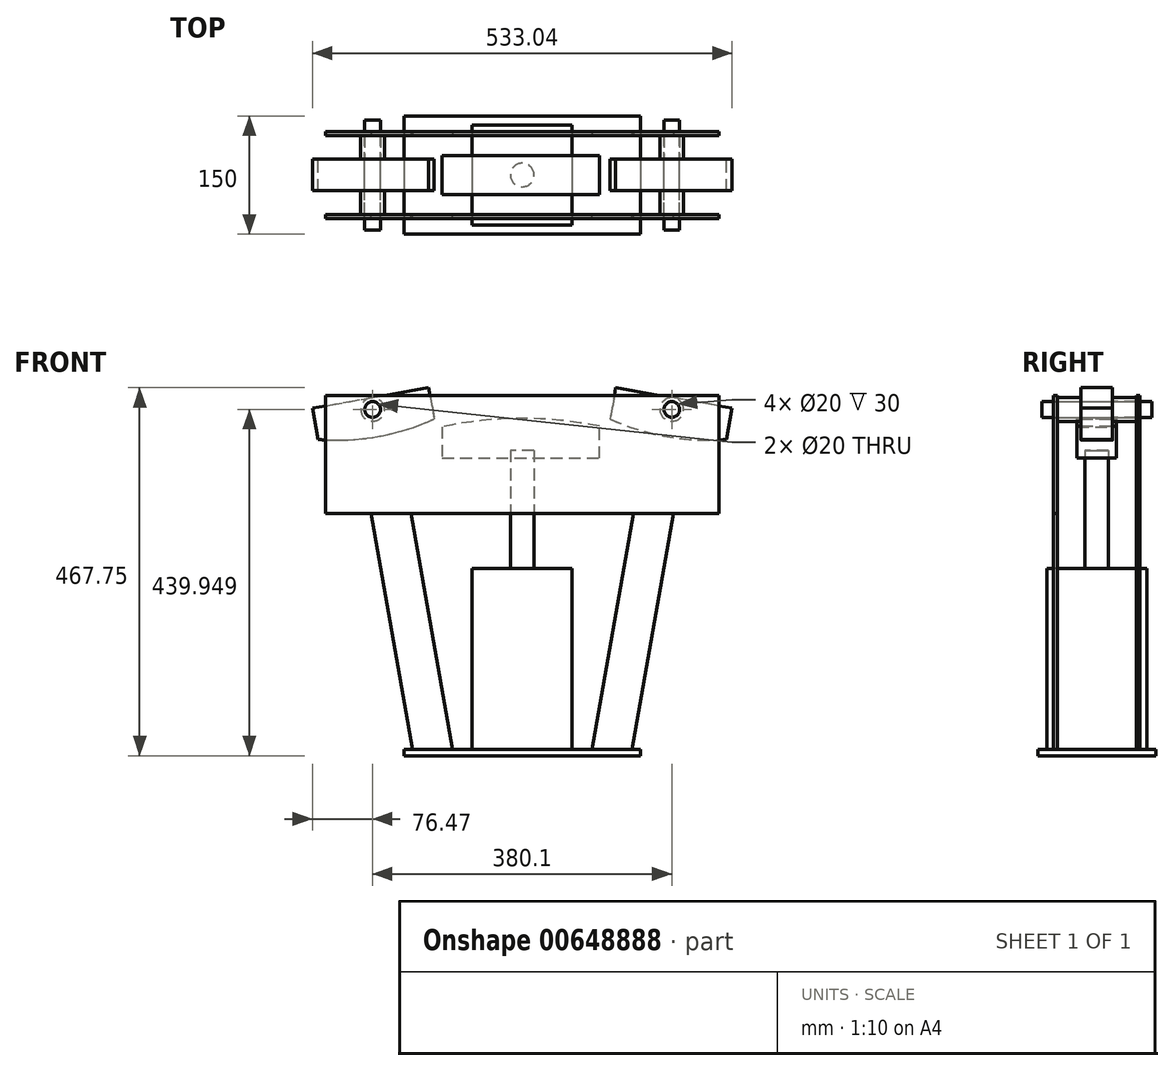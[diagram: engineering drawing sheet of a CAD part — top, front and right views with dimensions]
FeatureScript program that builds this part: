
annotation { "Feature Type Name" : "Feature", "Feature Type Description" : "" }
export const myFeature = defineFeature(function(context is Context, id is Id, definition is map)
    precondition{}
    {
        {
            var Q0;
            Q0=qCreatedBy(makeId("Top.planeOp"),FACE);
            cPlane(context, id + "F0", {"entities" : qUnion([Q0]), "cplaneType" : CPlaneType.OFFSET, "offset" : (250 + 127) * mm, "oppositeDirection" : true, "width" : 150 * mm, "height" : 150 * mm});
        }
        {
            var Q0;
            Q0=qCreatedBy(id+"F0.planeOp",FACE);
            var sketch = newSketch(context, id + "F1", { "sketchPlane" : qUnion([Q0])});
            skLineSegment(sketch, "E0.bottom", {"start": v(63.5, 63.5) * mm, "end": v(-63.5, 63.5) * mm});
            skLineSegment(sketch, "E0.top", {"start": v(63.5, -63.5) * mm, "end": v(-63.5, -63.5) * mm});
            skLineSegment(sketch, "E0.left", {"start": v(63.5, 63.5) * mm, "end": v(63.5, -63.5) * mm});
            skLineSegment(sketch, "E0.right", {"start": v(-63.5, 63.5) * mm, "end": v(-63.5, -63.5) * mm});
            skPoint(sketch, "E0.middle", {"position": v(0, 0) * mm});
            skSolve(sketch);
        }
        {
            var Q0;
            Q0=qSketchRegion(id+"F1",true);
            extrude(context, id + "F2", {"entities" : qUnion([Q0]), "depth" : 230 * mm, "offsetDistance" : 25 * mm});
        }
        {
            var Q0;
            Q0=makeQuery(id+"F2.opExtrude","CAP_FACE",FACE,{"disambiguationData":[OSD([sQuery(id+"F1.wireOp",EDGE,"E0.bottom"),sQuery(id+"F1.wireOp",EDGE,"E0.top"),sQuery(id+"F1.wireOp",EDGE,"E0.left"),sQuery(id+"F1.wireOp",EDGE,"E0.right")])],"isStart":false});
            var sketch = newSketch(context, id + "F3", { "sketchPlane" : qUnion([Q0])});
            skCircle(sketch, "E1", {"center": v(0, 0) * mm, "radius": 15 * mm});
            skSolve(sketch);
        }
        {
            var Q0;
            Q0=qSketchRegion(id+"F3",true);
            extrude(context, id + "F4", {"entities" : qUnion([Q0]), "depth" : 150 * mm, "offsetDistance" : 25 * mm});
        }
        {
            var Q0;
            Q0=qCreatedBy(id+"F0.planeOp",FACE);
            var sketch = newSketch(context, id + "F5", { "sketchPlane" : qUnion([Q0])});
            skLineSegment(sketch, "E2.bottom", {"start": v(150, 75) * mm, "end": v(-150, 75) * mm});
            skLineSegment(sketch, "E2.top", {"start": v(150, -75) * mm, "end": v(-150, -75) * mm});
            skLineSegment(sketch, "E2.left", {"start": v(150, 75) * mm, "end": v(150, -75) * mm});
            skLineSegment(sketch, "E2.right", {"start": v(-150, 75) * mm, "end": v(-150, -75) * mm});
            skPoint(sketch, "E2.middle", {"position": v(0, 0) * mm});
            skSolve(sketch);
        }
        {
            var Q0;
            Q0=qSketchRegion(id+"F5",true);
            extrude(context, id + "F6", {"entities" : qUnion([Q0]), "oppositeDirection" : true, "depth" : 8 * mm, "offsetDistance" : 25 * mm});
        }
        {
            var Q0;
            Q0=qCreatedBy(makeId("Front.planeOp"),FACE);
            var sketch = newSketch(context, id + "F7", { "sketchPlane" : qUnion([Q0])});
            skArc(sketch, "E3", {"start": v(-101.76, 33) * mm, "mid": v(-1.8, 43.46) * mm, "end": v(98.24, 33.72) * mm});
            skLineSegment(sketch, "E4", {"start": v(-101.76, 33) * mm, "end": v(-101.76, -7) * mm});
            skLineSegment(sketch, "E5", {"start": v(-101.76, -7) * mm, "end": v(98.24, -7) * mm});
            skLineSegment(sketch, "E6", {"start": v(98.24, -7) * mm, "end": v(98.24, 33.72) * mm});
            skSolve(sketch);
        }
        {
            var Q0;
            Q0 = qSketchRegion(id + "F7", true);
            extrude(context, id + "F8", {"entities" : qUnion([Q0]), "endBound" : BoundingType.SYMMETRIC, "depth" : 50 * mm, "offsetDistance" : 25 * mm});
        }
        {
            var Q0;
            Q0=qCreatedBy(makeId("Front.planeOp"),FACE);
            cPlane(context, id + "F9", {"entities" : qUnion([Q0]), "cplaneType" : CPlaneType.OFFSET, "offset" : 50 * mm, "width" : 150 * mm, "height" : 150 * mm});
        }
        {
            var Q0;
            Q0=qCreatedBy(id+"F9.planeOp",FACE);
            var sketch = newSketch(context, id + "F10", { "sketchPlane" : qUnion([Q0])});
            skLineSegment(sketch, "E7", {"start": v(-88.5, -377) * mm, "end": v(-141.4, -77) * mm});
            skLineSegment(sketch, "E8", {"start": v(-141.4, -77) * mm, "end": v(-192.17, -77) * mm});
            skLineSegment(sketch, "E9", {"start": v(-192.17, -77) * mm, "end": v(-139.27, -377) * mm});
            skLineSegment(sketch, "E10", {"start": v(-139.27, -377) * mm, "end": v(-88.5, -377) * mm});
            skSolve(sketch);
        }
        {
            var Q0;
            Q0 = qSketchRegion(id + "F10", true);
            extrude(context, id + "F11", {"entities" : qUnion([Q0]), "depth" : 5 * mm, "offsetDistance" : 25 * mm});
        }
        {
            var Q0;
            Q0=makeQuery(id+"F11.opExtrude","SWEPT_BODY",BODY,{"disambiguationData":[OSD([sQuery(id+"F10.wireOp",EDGE,"E7"),sQuery(id+"F10.wireOp",EDGE,"E8"),sQuery(id+"F10.wireOp",EDGE,"E9"),sQuery(id+"F10.wireOp",EDGE,"E10")])]});
            var Q1;
            Q1=qCreatedBy(makeId("Front.planeOp"),FACE);
            mirror(context, id + "F12", {"entities" : qUnion([Q0]), "mirrorPlane" : qUnion([Q1])});
        }
        {
            var Q0;
            Q0=makeQuery(id+"F12.opPattern","COPY",BODY,{"derivedFrom":makeQuery(id+"F11.opExtrude","SWEPT_BODY",BODY,{"disambiguationData":[OSD([sQuery(id+"F10.wireOp",EDGE,"E7"),sQuery(id+"F10.wireOp",EDGE,"E8"),sQuery(id+"F10.wireOp",EDGE,"E9"),sQuery(id+"F10.wireOp",EDGE,"E10")])]}),"instanceName":"1"});
            var Q1;
            Q1=makeQuery(id+"F11.opExtrude","SWEPT_BODY",BODY,{"disambiguationData":[OSD([sQuery(id+"F10.wireOp",EDGE,"E7"),sQuery(id+"F10.wireOp",EDGE,"E8"),sQuery(id+"F10.wireOp",EDGE,"E9"),sQuery(id+"F10.wireOp",EDGE,"E10")])]});
            var Q2;
            Q2=qCreatedBy(makeId("Right.planeOp"),FACE);
            mirror(context, id + "F13", {"entities" : qUnion([Q0, Q1]), "mirrorPlane" : qUnion([Q2])});
        }
        {
            var Q0;
            Q0=qCreatedBy(id+"F9.planeOp",FACE);
            var sketch = newSketch(context, id + "F14", { "sketchPlane" : qUnion([Q0])});
            skLineSegment(sketch, "E11.bottom", {"start": v(250, -77) * mm, "end": v(-250, -77) * mm});
            skLineSegment(sketch, "E11.top", {"start": v(250, 73) * mm, "end": v(-250, 73) * mm});
            skLineSegment(sketch, "E11.left", {"start": v(250, -77) * mm, "end": v(250, 73) * mm});
            skLineSegment(sketch, "E11.right", {"start": v(-250, -77) * mm, "end": v(-250, 73) * mm});
            skPoint(sketch, "E11.middle", {"position": v(0, -2) * mm});
            skSolve(sketch);
        }
        {
            var Q0;
            Q0 = qSketchRegion(id + "F14", true);
            extrude(context, id + "F15", {"entities" : qUnion([Q0]), "depth" : 5 * mm, "offsetDistance" : 25 * mm});
        }
        {
            var Q0;
            Q0=makeQuery(id+"F15.opExtrude","SWEPT_BODY",BODY,{"disambiguationData":[OSD([sQuery(id+"F14.wireOp",EDGE,"E11.bottom"),sQuery(id+"F14.wireOp",EDGE,"E11.top"),sQuery(id+"F14.wireOp",EDGE,"E11.left"),sQuery(id+"F14.wireOp",EDGE,"E11.right")])]});
            var Q1;
            Q1=qCreatedBy(makeId("Front.planeOp"),FACE);
            mirror(context, id + "F16", {"entities" : qUnion([Q0]), "mirrorPlane" : qUnion([Q1])});
        }
        {
            var Q0;
            Q0=qCreatedBy(makeId("Front.planeOp"),FACE);
            var sketch = newSketch(context, id + "F17", { "sketchPlane" : qUnion([Q0])});
            skLineSegment(sketch, "E12", {"start": v(-266.52, 56.7) * mm, "end": v(-118.8, 82.75) * mm});
            skLineSegment(sketch, "E13", {"start": v(-118.8, 82.75) * mm, "end": v(-111.77, 42.89) * mm});
            skLineSegment(sketch, "E14", {"start": v(-266.52, 56.7) * mm, "end": v(-259.49, 16.84) * mm});
            skLineSegment(sketch, "E15", {"start": v(-202.42, 125.11) * mm, "end": v(-151.73, -162.4) * mm, "construction": true});
            skLineSegment(sketch, "E16", {"start": v(-202.42, 125.11) * mm, "end": v(-236.07, 315.92) * mm, "construction": true});
            skArc(sketch, "E17", {"start": v(-259.49, 16.84) * mm, "mid": v(-183.97, 20.48) * mm, "end": v(-111.77, 42.89) * mm});
            skCircle(sketch, "E18.0", {"center": v(-190.05, 54.95) * mm, "radius": 10 * mm});
            skSolve(sketch);
        }
        {
            var Q0;
            Q0=makeQuery(id+"F17.imprint","IMPRINT",FACE,{"disambiguationData":[TD([[makeQuery(id+"F17.imprint","IMPRINT",EDGE,{"derivedFrom":sQuery(id+"F17.wireOp",EDGE,"E12")}),-1.0]])]});
            extrude(context, id + "F18", {"entities" : qUnion([Q0]), "endBound" : BoundingType.SYMMETRIC, "depth" : 40 * mm, "offsetDistance" : 25 * mm});
        }
        {
            var Q0;
            Q0=makeQuery(id+"F18.opExtrude","CAP_FACE",FACE,{"disambiguationData":[OSD([sQuery(id+"F17.wireOp",EDGE,"E12"),sQuery(id+"F17.wireOp",EDGE,"E13"),sQuery(id+"F17.wireOp",EDGE,"E14"),sQuery(id+"F17.wireOp",EDGE,"E17"),sQuery(id+"F17.wireOp",EDGE,"E18.0")])],"isStart":false});
            var sketch = newSketch(context, id + "F19", { "sketchPlane" : qUnion([Q0])});
            skCircle(sketch, "E19.0", {"center": v(-190.05, 54.95) * mm, "radius": 10 * mm});
            skCircle(sketch, "E20", {"center": v(-190.05, 54.95) * mm, "radius": 15 * mm});
            skSolve(sketch);
        }
        {
            var Q0;
            Q0 = qSketchRegion(id + "F19", true);
            extrude(context, id + "F20", {"entities" : qUnion([Q0]), "endBound" : BoundingType.UP_TO_NEXT, "depth" : 25 * mm, "offsetDistance" : 25 * mm});
        }
        {
            var Q0;
            Q0=makeQuery(id+"F20.opExtrude","SWEPT_BODY",BODY,{"disambiguationData":[OSD([sQuery(id+"F19.wireOp",EDGE,"E19.0"),sQuery(id+"F19.wireOp",EDGE,"E20")])]});
            var Q1;
            Q1=qCreatedBy(makeId("Front.planeOp"),FACE);
            mirror(context, id + "F21", {"entities" : qUnion([Q0]), "mirrorPlane" : qUnion([Q1])});
        }
        {
            var Q0;
            Q0=makeQuery(id+"F11.opExtrude","CAP_FACE",FACE,{"disambiguationData":[OSD([sQuery(id+"F10.wireOp",EDGE,"E7"),sQuery(id+"F10.wireOp",EDGE,"E8"),sQuery(id+"F10.wireOp",EDGE,"E9"),sQuery(id+"F10.wireOp",EDGE,"E10")])],"isStart":false});
            var sketch = newSketch(context, id + "F22", { "sketchPlane" : qUnion([Q0])});
            skCircle(sketch, "E21.0", {"center": v(-190.05, 54.95) * mm, "radius": 10 * mm});
            skSolve(sketch);
        }
        {
            var Q0;
            Q0 = qSketchRegion(id + "F22", true);
            extrude(context, id + "F23", {"entities" : qUnion([Q0]), "depth" : 15 * mm, "offsetDistance" : 25 * mm, "hasSecondDirection" : true, "secondDirectionOppositeDirection" : true, "secondDirectionDepth" : 125 * mm});
        }
        {
            var Q0;
            Q0=makeQuery(id+"F23.opExtrude","SWEPT_BODY",BODY,{"disambiguationData":[OSD([sQuery(id+"F22.wireOp",EDGE,"E21.0")])]});
            var Q1;
            Q1=makeQuery(id+"F20.opExtrude","SWEPT_BODY",BODY,{"disambiguationData":[OSD([sQuery(id+"F19.wireOp",EDGE,"E19.0"),sQuery(id+"F19.wireOp",EDGE,"E20")])]});
            var Q2;
            Q2=makeQuery(id+"F21.opPattern","COPY",BODY,{"derivedFrom":makeQuery(id+"F20.opExtrude","SWEPT_BODY",BODY,{"disambiguationData":[OSD([sQuery(id+"F19.wireOp",EDGE,"E19.0"),sQuery(id+"F19.wireOp",EDGE,"E20")])]}),"instanceName":"1"});
            var Q3;
            Q3=makeQuery(id+"F18.opExtrude","SWEPT_BODY",BODY,{"disambiguationData":[OSD([sQuery(id+"F17.wireOp",EDGE,"E12"),sQuery(id+"F17.wireOp",EDGE,"E13"),sQuery(id+"F17.wireOp",EDGE,"E14"),sQuery(id+"F17.wireOp",EDGE,"E17"),sQuery(id+"F17.wireOp",EDGE,"E18.0")])]});
            var Q4;
            Q4=qCreatedBy(makeId("Right.planeOp"),FACE);
            mirror(context, id + "F24", {"entities" : qUnion([Q0, Q1, Q2, Q3]), "mirrorPlane" : qUnion([Q4])});
        }
    });
